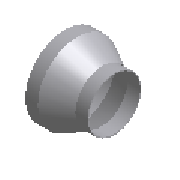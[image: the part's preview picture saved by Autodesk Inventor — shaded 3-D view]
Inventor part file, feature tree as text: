
AUTODESK INVENTOR PART (.ipt)
format: ipt  version: 2023.2 (Build 272271030, 271C)  size: 171,520 bytes
history: native  units: mm (DEFAULTED — no unit token found)
features: other x4, revolve x1, sketch x1
ambient origin geometry x8: Origin, YZ Plane, XZ Plane, XY Plane, X Axis, Y Axis, Z Axis, Center Point
bodies: Solid1 (feature_tree)
feature tree (6):
  revolve  "Revolution1"  [1 undecoded]
  other  "Work Axis1"
  other  "Work Point1"
  other  "Work Axis2"
  other  "Work Point2"
  sketch  "Sketch1"  dims[d0=114.3mm d1=88.9mm d2=2.0mm d3=2.0mm d4=102.0mm d5=25.5mm d6=25.5mm d7=2.0mm d9=90.0deg]
note: 1 required parameter value undecoded (feature->parameter linkage not recoverable at this tier; creation-order binding heuristic only, values carry confidence <= 0.55)
